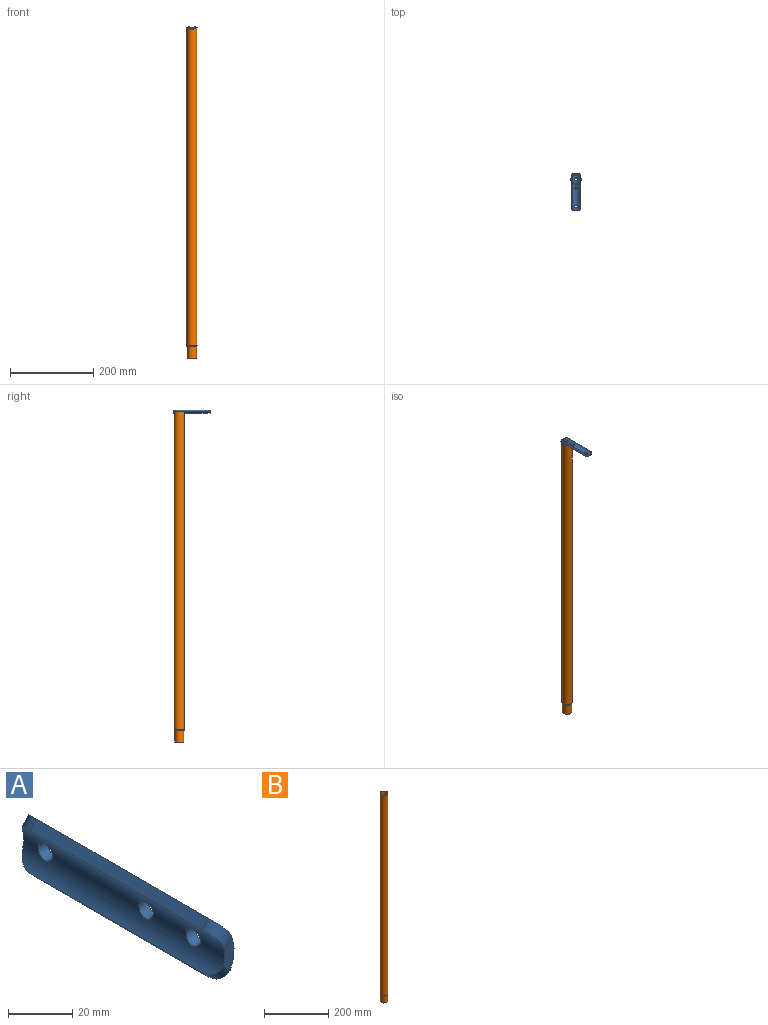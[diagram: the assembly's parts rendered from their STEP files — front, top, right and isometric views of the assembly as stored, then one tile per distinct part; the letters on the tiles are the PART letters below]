
ASSEMBLY  parts=2 mates=1
PART A: 13 faces, bbox 9x88.9x22.4 mm
  f0: cylinder r=11.18mm len=88.9mm, axis (0,1,0), area 1505.3mm2, adj f2,f3,f4,f5,f6,f7,f8,f9
  f1: cylinder r=15.24mm len=88.9mm, axis (0,1,0), area 2100.8mm2, adj f2,f3,f4,f5,f6,f7,f8,f9
  f2: plane 76.32x2.98mm, normal (-0.73,0,-0.68), area 310.2mm2, adj f0,f1,f8,f9
  f3: plane 12.89x4.73mm, normal (0,-1,0), area 40mm2, adj f0,f1,f6,f8
  f4: plane 11.69x4.33mm, normal (0,1,0), area 34.5mm2, adj f0,f1,f7,f9
  f5: plane 76.2x2.98mm, normal (-0.73,0,0.68), area 309.7mm2, adj f0,f1,f6,f7
  f6: cylinder r=6.35mm len=8.77mm, axis (0.68,0,0.73), area 41.8mm2, adj f0,f1,f3,f5
  f7: cylinder r=6.35mm len=8.77mm, axis (0.68,0,0.73), area 41.8mm2, adj f0,f1,f4,f5
  f8: cylinder r=6.35mm len=7.37mm, axis (0.68,0,-0.73), area 36.2mm2, adj f0,f1,f2,f3
  f9: cylinder r=6.35mm len=8.77mm, axis (0.68,0,-0.73), area 41.8mm2, adj f0,f1,f2,f4
  f10: cylinder r=3.17mm len=6.35mm, axis (-1,0,0), area 82.3mm2, adj f0,f1
  f11: cylinder r=3.17mm len=6.35mm, axis (-1,0,0), area 82.3mm2, adj f0,f1
  f12: cylinder r=3.17mm len=6.35mm, axis (-1,0,0), area 82.3mm2, adj f0,f1
PART B: 10 faces, bbox 26.5x26.5x793.5 mm
  f0: cylinder r=10.41mm len=764.34mm, axis (0,0,-1), area 50013mm2, adj f1,f9
  f1: torus R=8.64mm, axis (0,0,-1), area 88.7mm2, adj f0,f2
  f2: torus R=11.18mm, axis (0,0,-1), area 82.9mm2, adj f1,f3
  f3: cylinder r=9.4mm len=26.67mm, axis (0,0,-1), area 1574.8mm2, adj f2,f4
  f4: plane 22.45x22.45mm, normal (0,0,-1), area 118.4mm2, adj f3,f5
  f5: cylinder r=11.23mm len=26.67mm, axis (0,0,-1), area 1881mm2, adj f4,f6
  f6: torus R=13mm, axis (0,0,-1), area 98.7mm2, adj f5,f7
  f7: torus R=10.46mm, axis (0,0,-1), area 104.5mm2, adj f6,f8
  f8: cylinder r=12.24mm len=764.34mm, axis (0,0,-1), area 58787.8mm2, adj f7,f9
  f9: plane 24.48x24.48mm, normal (0,0,1), area 130mm2, adj f0,f8
PLACE A rot(axis=(0.71,0,-0.71),180deg) t=(65.16,-244.32,105.7)mm
PLACE B t=(65.16,-169.39,-699.25)mm
MATE revolute A.f10 <-> B.f0  axis (0,0,1) through (65.16,-169.39,90.43)mm
